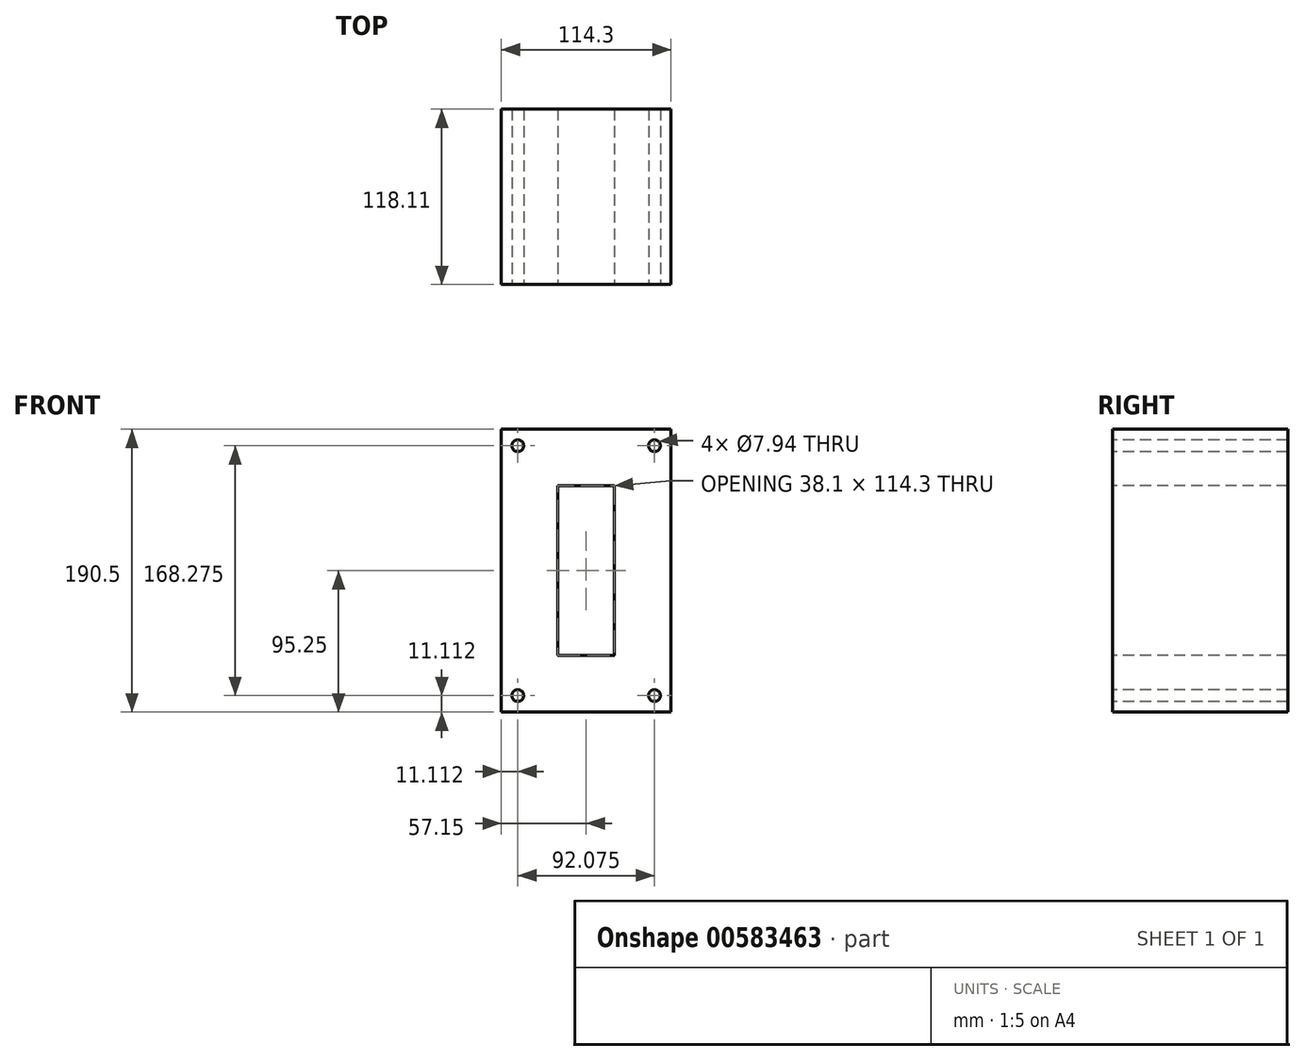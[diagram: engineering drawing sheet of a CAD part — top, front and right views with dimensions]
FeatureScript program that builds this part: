
annotation { "Feature Type Name" : "Feature", "Feature Type Description" : "" }
export const myFeature = defineFeature(function(context is Context, id is Id, definition is map)
    precondition{}
    {
        {
            assignVariable(context, id + "F0", {"name" : "StackHeight", "anyValue" : 118.11 * mm});
        }
        {
            var Q0;
            Q0=qCreatedBy(makeId("Front.planeOp"),FACE);
            var sketch = newSketch(context, id + "F1", { "sketchPlane" : qUnion([Q0])});
            skLineSegment(sketch, "E0.bottom", {"start": v(57.15, -95.25) * mm, "end": v(-57.15, -95.25) * mm});
            skLineSegment(sketch, "E0.top", {"start": v(57.15, 95.25) * mm, "end": v(-57.15, 95.25) * mm});
            skLineSegment(sketch, "E0.left", {"start": v(57.15, -95.25) * mm, "end": v(57.15, 95.25) * mm});
            skLineSegment(sketch, "E0.right", {"start": v(-57.15, -95.25) * mm, "end": v(-57.15, 95.25) * mm});
            skPoint(sketch, "E0.middle", {"position": v(0, 0) * mm});
            skSolve(sketch);
        }
        {
            var Q0;
            Q0=qSketchRegion(id+"F1",true);
            extrude(context, id + "F2", {"entities" : qUnion([Q0]), "oppositeDirection" : true, "depth" : getVariable(context, 'StackHeight')});
        }
        {
            var Q0;
            Q0=makeQuery(id+"F2.opExtrude","CAP_FACE",FACE,{"disambiguationData":[OSD([sQuery(id+"F1.wireOp",EDGE,"E0.bottom"),sQuery(id+"F1.wireOp",EDGE,"E0.top"),sQuery(id+"F1.wireOp",EDGE,"E0.left"),sQuery(id+"F1.wireOp",EDGE,"E0.right")])],"isStart":true});
            var sketch = newSketch(context, id + "F3", { "sketchPlane" : qUnion([Q0])});
            skCircle(sketch, "E1", {"center": v(-46.04, 84.14) * mm, "radius": 3.97 * mm});
            skCircle(sketch, "E2", {"center": v(46.04, 84.14) * mm, "radius": 3.97 * mm});
            skCircle(sketch, "E3", {"center": v(-46.04, -84.14) * mm, "radius": 3.97 * mm});
            skCircle(sketch, "E4", {"center": v(46.04, -84.14) * mm, "radius": 3.97 * mm});
            skSolve(sketch);
        }
        {
            var Q0;
            Q0=qSketchRegion(id+"F3",true);
            extrude(context, id + "F4", {"entities" : qUnion([Q0]), "operationType" : NewBodyOperationType.REMOVE, "oppositeDirection" : true, "depth" : getVariable(context, 'StackHeight')});
        }
        {
            var Q0;
            Q0=makeQuery(id+"F2.opExtrude","CAP_FACE",FACE,{"disambiguationData":[OSD([sQuery(id+"F1.wireOp",EDGE,"E0.bottom"),sQuery(id+"F1.wireOp",EDGE,"E0.top"),sQuery(id+"F1.wireOp",EDGE,"E0.left"),sQuery(id+"F1.wireOp",EDGE,"E0.right")])],"isStart":true});
            var sketch = newSketch(context, id + "F5", { "sketchPlane" : qUnion([Q0])});
            skLineSegment(sketch, "E5.bottom", {"start": v(-19.05, -57.15) * mm, "end": v(19.05, -57.15) * mm});
            skLineSegment(sketch, "E5.top", {"start": v(-19.05, 57.15) * mm, "end": v(19.05, 57.15) * mm});
            skLineSegment(sketch, "E5.left", {"start": v(-19.05, -57.15) * mm, "end": v(-19.05, 57.15) * mm});
            skLineSegment(sketch, "E5.right", {"start": v(19.05, -57.15) * mm, "end": v(19.05, 57.15) * mm});
            skPoint(sketch, "E5.middle", {"position": v(0, 0) * mm});
            skSolve(sketch);
        }
        {
            var Q0;
            Q0=qSketchRegion(id+"F5",true);
            extrude(context, id + "F6", {"entities" : qUnion([Q0]), "operationType" : NewBodyOperationType.REMOVE, "oppositeDirection" : true, "depth" : getVariable(context, 'StackHeight')});
        }
        {
            var Q0;
            Q0=makeQuery(id+"F6.boolean.opBoolean","COPY",EDGE,{"derivedFrom":makeQuery(id+"F6.opExtrude","SWEPT_EDGE",EDGE,{"disambiguationData":[OSD([sQuery(id+"F5.wireOp",EDGE,"E5.top"),sQuery(id+"F5.wireOp",EDGE,"E5.left")])]})});
            var Q1;
            Q1=makeQuery(id+"F6.boolean.opBoolean","COPY",EDGE,{"derivedFrom":makeQuery(id+"F6.opExtrude","SWEPT_EDGE",EDGE,{"disambiguationData":[OSD([sQuery(id+"F5.wireOp",EDGE,"E5.top"),sQuery(id+"F5.wireOp",EDGE,"E5.right")])]})});
            var Q2;
            Q2=makeQuery(id+"F6.boolean.opBoolean","COPY",EDGE,{"derivedFrom":makeQuery(id+"F6.opExtrude","SWEPT_EDGE",EDGE,{"disambiguationData":[OSD([sQuery(id+"F5.wireOp",EDGE,"E5.bottom"),sQuery(id+"F5.wireOp",EDGE,"E5.right")])]})});
            var Q3;
            Q3=makeQuery(id+"F6.boolean.opBoolean","COPY",EDGE,{"derivedFrom":makeQuery(id+"F6.opExtrude","SWEPT_EDGE",EDGE,{"disambiguationData":[OSD([sQuery(id+"F5.wireOp",EDGE,"E5.bottom"),sQuery(id+"F5.wireOp",EDGE,"E5.left")])]})});
            fillet(context, id + "F7", {"entities" : qUnion([Q0, Q1, Q2, Q3]), "radius" : 0.25 * mm, "tangentPropagation" : true, "allowEdgeOverflow" : false});
        }
    });
